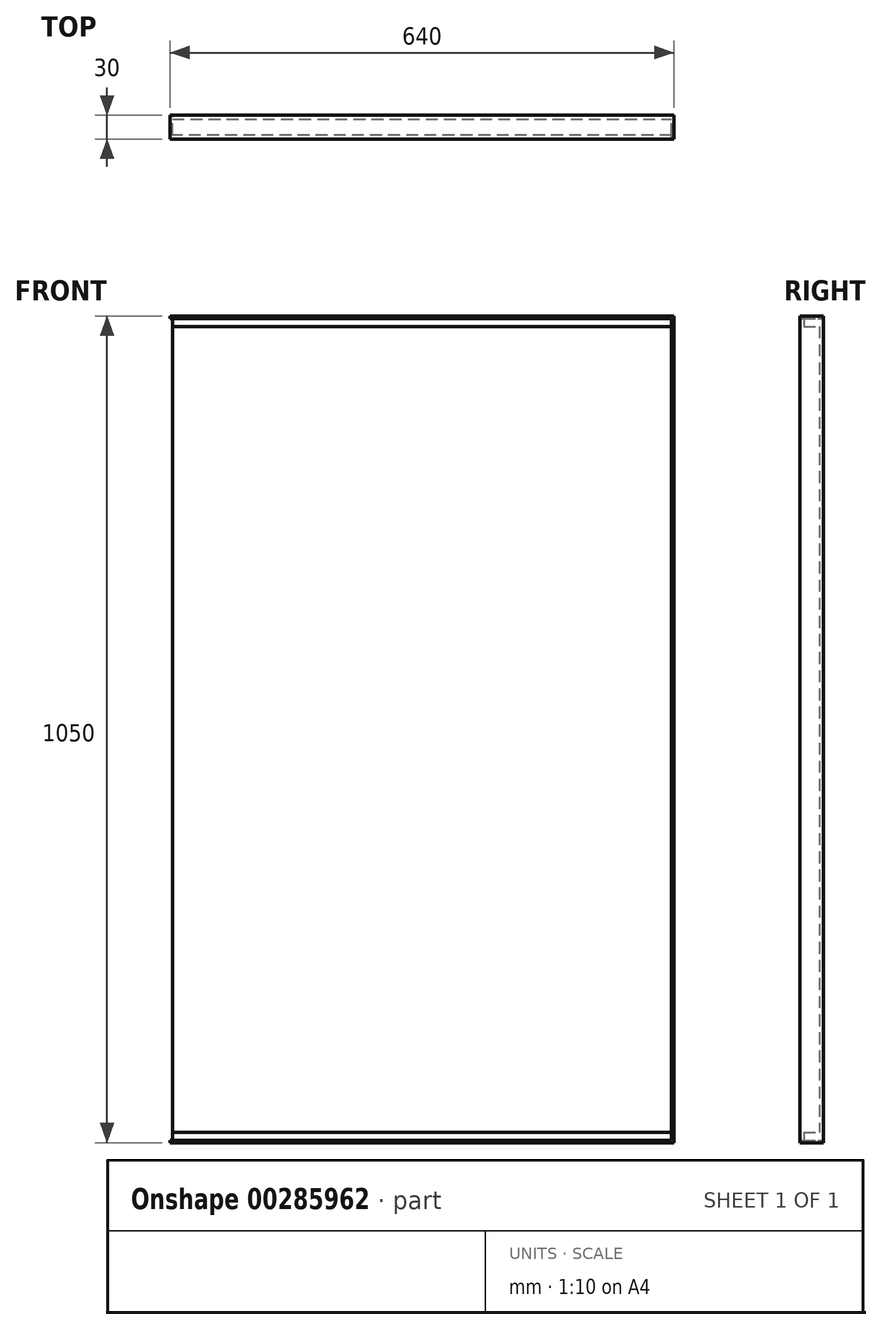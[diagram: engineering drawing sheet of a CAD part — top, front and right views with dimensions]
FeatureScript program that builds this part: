
annotation { "Feature Type Name" : "Feature", "Feature Type Description" : "" }
export const myFeature = defineFeature(function(context is Context, id is Id, definition is map)
    precondition{}
    {
        {
            var Q0;
            Q0=qCreatedBy(makeId("Front.planeOp"),FACE);
            var sketch = newSketch(context, id + "F0", { "sketchPlane" : qUnion([Q0])});
            skLineSegment(sketch, "E0.bottom", {"start": v(0, -1044) * mm, "end": v(3, -1044) * mm});
            skLineSegment(sketch, "E0.top", {"start": v(0, 0) * mm, "end": v(3, 0) * mm});
            skLineSegment(sketch, "E0.left", {"start": v(0, -1044) * mm, "end": v(0, 0) * mm});
            skLineSegment(sketch, "E0.right", {"start": v(3, -1044) * mm, "end": v(3, 0) * mm});
            skLineSegment(sketch, "E1.bottom", {"start": v(3, 0) * mm, "end": v(-637, 0) * mm});
            skLineSegment(sketch, "E1.top", {"start": v(3, 3) * mm, "end": v(-637, 3) * mm});
            skLineSegment(sketch, "E1.left", {"start": v(3, 0) * mm, "end": v(3, 3) * mm});
            skLineSegment(sketch, "E1.right", {"start": v(-637, 0) * mm, "end": v(-637, 3) * mm});
            skLineSegment(sketch, "E2.bottom", {"start": v(-637, 0) * mm, "end": v(-634, 0) * mm});
            skLineSegment(sketch, "E2.top", {"start": v(-637, -1044) * mm, "end": v(-634, -1044) * mm});
            skLineSegment(sketch, "E2.left", {"start": v(-637, 0) * mm, "end": v(-637, -1044) * mm});
            skLineSegment(sketch, "E2.right", {"start": v(-634, 0) * mm, "end": v(-634, -1044) * mm});
            skLineSegment(sketch, "E3.bottom", {"start": v(-637, -1044) * mm, "end": v(3, -1044) * mm});
            skLineSegment(sketch, "E3.top", {"start": v(-637, -1047) * mm, "end": v(3, -1047) * mm});
            skLineSegment(sketch, "E3.left", {"start": v(-637, -1044) * mm, "end": v(-637, -1047) * mm});
            skLineSegment(sketch, "E3.right", {"start": v(3, -1044) * mm, "end": v(3, -1047) * mm});
            skSolve(sketch);
        }
        {
            var Q0;
            Q0=makeQuery(id+"F0.imprint","IMPRINT",FACE,{"disambiguationData":[TD([[makeQuery(id+"F0.imprint","IMPRINT",EDGE,{"derivedFrom":sQuery(id+"F0.wireOp",EDGE,"E1.top")}),1.0]])]});
            var Q1;
            {var subQ0=sQuery(id+"F0.wireOp",EDGE,"E0.left");Q1=makeQuery(id+"F0.imprint","IMPRINT",FACE,{"disambiguationData":[TD([[makeQuery(id+"F0.imprint","IMPRINT",EDGE,{"derivedFrom":subQ0}),-1.0]])]});}
            var Q2;
            Q2=makeQuery(id+"F0.imprint","IMPRINT",FACE,{"disambiguationData":[TD([[makeQuery(id+"F0.imprint","IMPRINT",EDGE,{"derivedFrom":sQuery(id+"F0.wireOp",EDGE,"E2.bottom")}),-1.0]])]});
            var Q3;
            Q3=makeQuery(id+"F0.imprint","IMPRINT",FACE,{"disambiguationData":[TD([[makeQuery(id+"F0.imprint","IMPRINT",EDGE,{"derivedFrom":sQuery(id+"F0.wireOp",EDGE,"E3.top")}),1.0]])]});
            extrude(context, id + "F1", {"entities" : qUnion([Q0, Q1, Q2, Q3]), "depth" : 30 * mm});
        }
        {
            var Q0;
            Q0=qCreatedBy(makeId("Front.planeOp"),FACE);
            var sketch = newSketch(context, id + "F2", { "sketchPlane" : qUnion([Q0])});
            skLineSegment(sketch, "E4.bottom", {"start": v(0, 0) * mm, "end": v(-634, 0) * mm});
            skLineSegment(sketch, "E4.top", {"start": v(0, -1044) * mm, "end": v(-634, -1044) * mm});
            skLineSegment(sketch, "E4.left", {"start": v(0, 0) * mm, "end": v(0, -1044) * mm});
            skLineSegment(sketch, "E4.right", {"start": v(-634, 0) * mm, "end": v(-634, -1044) * mm});
            skSolve(sketch);
        }
        {
            var Q0;
            Q0=makeQuery(id+"F2.imprint","IMPRINT",FACE,{"disambiguationData":[TD([[makeQuery(id+"F2.imprint","IMPRINT",EDGE,{"derivedFrom":sQuery(id+"F2.wireOp",EDGE,"E4.bottom")}),1.0]])]});
            extrude(context, id + "F3", {"entities" : qUnion([Q0]), "operationType" : NewBodyOperationType.ADD, "depth" : 5 * mm});
        }
        {
            var Q0;
            Q0=makeQuery(id+"F3.opExtrude","CAP_FACE",FACE,{"disambiguationData":[OSD([sQuery(id+"F2.wireOp",EDGE,"E4.bottom"),sQuery(id+"F2.wireOp",EDGE,"E4.top"),sQuery(id+"F2.wireOp",EDGE,"E4.left"),sQuery(id+"F2.wireOp",EDGE,"E4.right")])],"isStart":false});
            var sketch = newSketch(context, id + "F4", { "sketchPlane" : qUnion([Q0])});
            skLineSegment(sketch, "E5.bottom", {"start": v(0, 0) * mm, "end": v(-634, 0) * mm});
            skLineSegment(sketch, "E5.top", {"start": v(0, -10) * mm, "end": v(-634, -10) * mm});
            skLineSegment(sketch, "E5.left", {"start": v(0, 0) * mm, "end": v(0, -10) * mm});
            skLineSegment(sketch, "E5.right", {"start": v(-634, 0) * mm, "end": v(-634, -10) * mm});
            skLineSegment(sketch, "E6.bottom", {"start": v(-634, -10) * mm, "end": v(-624, -10) * mm});
            skLineSegment(sketch, "E6.top", {"start": v(-634, -1034) * mm, "end": v(-624, -1034) * mm});
            skLineSegment(sketch, "E6.left", {"start": v(-634, -10) * mm, "end": v(-634, -1034) * mm});
            skLineSegment(sketch, "E6.right", {"start": v(-624, -10) * mm, "end": v(-624, -1034) * mm});
            skLineSegment(sketch, "E7.bottom", {"start": v(-634, -1034) * mm, "end": v(0, -1034) * mm});
            skLineSegment(sketch, "E7.top", {"start": v(-634, -1044) * mm, "end": v(0, -1044) * mm});
            skLineSegment(sketch, "E7.left", {"start": v(-634, -1034) * mm, "end": v(-634, -1044) * mm});
            skLineSegment(sketch, "E7.right", {"start": v(0, -1034) * mm, "end": v(0, -1044) * mm});
            skLineSegment(sketch, "E8.bottom", {"start": v(0, -1034) * mm, "end": v(-10, -1034) * mm});
            skLineSegment(sketch, "E8.top", {"start": v(0, -10) * mm, "end": v(-10, -10) * mm});
            skLineSegment(sketch, "E8.left", {"start": v(0, -1034) * mm, "end": v(0, -10) * mm});
            skLineSegment(sketch, "E8.right", {"start": v(-10, -1034) * mm, "end": v(-10, -10) * mm});
            skSolve(sketch);
        }
        {
            var Q0;
            Q0=makeQuery(id+"F4.imprint","IMPRINT",FACE,{"disambiguationData":[TD([[makeQuery(id+"F4.imprint","IMPRINT",EDGE,{"derivedFrom":sQuery(id+"F4.wireOp",EDGE,"E5.bottom")}),1.0]])]});
            var Q1;
            Q1=makeQuery(id+"F4.imprint","IMPRINT",FACE,{"disambiguationData":[TD([[makeQuery(id+"F4.imprint","IMPRINT",EDGE,{"derivedFrom":sQuery(id+"F4.wireOp",EDGE,"E6.bottom")}),-1.0]])]});
            var Q2;
            Q2=makeQuery(id+"F4.imprint","IMPRINT",FACE,{"disambiguationData":[TD([[makeQuery(id+"F4.imprint","IMPRINT",EDGE,{"derivedFrom":sQuery(id+"F4.wireOp",EDGE,"E7.top")}),-1.0]])]});
            var Q3;
            Q3=makeQuery(id+"F4.imprint","IMPRINT",FACE,{"disambiguationData":[TD([[makeQuery(id+"F4.imprint","IMPRINT",EDGE,{"derivedFrom":sQuery(id+"F4.wireOp",EDGE,"E8.bottom")}),-1.0]])]});
            extrude(context, id + "F5", {"entities" : qUnion([Q0, Q1, Q2, Q3]), "operationType" : NewBodyOperationType.ADD, "depth" : 20 * mm});
        }
    });
